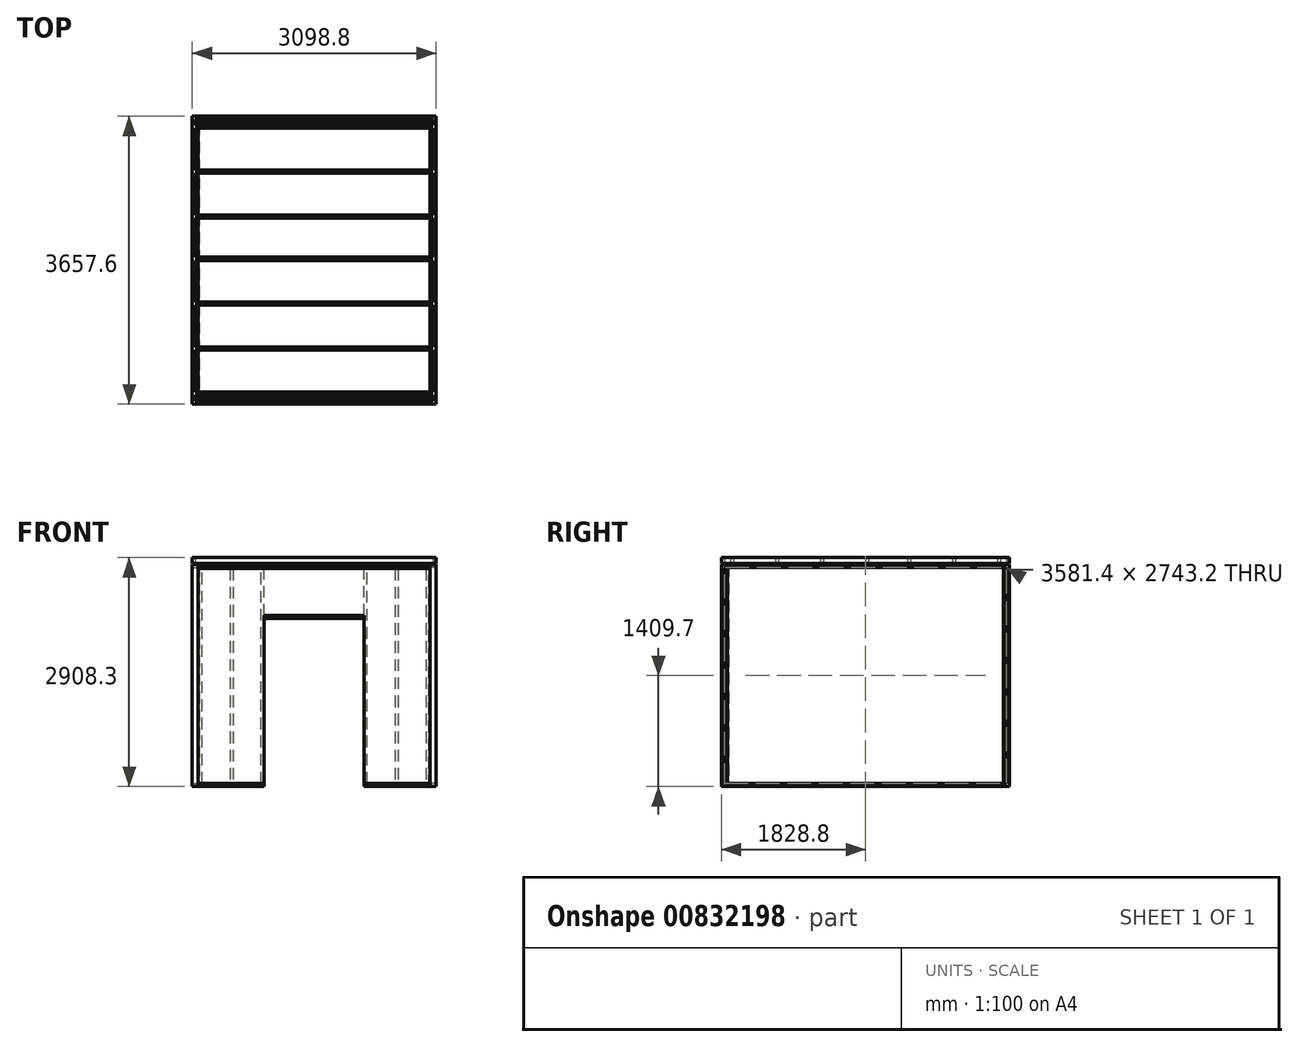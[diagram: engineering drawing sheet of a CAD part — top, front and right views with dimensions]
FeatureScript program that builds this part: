
annotation { "Feature Type Name" : "Feature", "Feature Type Description" : "" }
export const myFeature = defineFeature(function(context is Context, id is Id, definition is map)
    precondition{}
    {
        {
            var Q0;
            Q0=qCreatedBy(makeId("Top.planeOp"),FACE);
            var sketch = newSketch(context, id + "F0", { "sketchPlane" : qUnion([Q0])});
            skLineSegment(sketch, "E0.bottom", {"start": v(-980.79, 2857.66) * mm, "end": v(155.93, 2857.66) * mm});
            skLineSegment(sketch, "E0.top", {"start": v(-980.79, -622.14) * mm, "end": v(1105.1, -622.14) * mm});
            skLineSegment(sketch, "E0.left", {"start": v(-980.79, 2857.66) * mm, "end": v(-980.79, -622.14) * mm});
            skLineSegment(sketch, "E0.right", {"start": v(1940.21, 2857.66) * mm, "end": v(1940.21, -622.14) * mm});
            skLineSegment(sketch, "E1.bottom", {"start": v(-993.49, 2870.36) * mm, "end": v(155.93, 2870.36) * mm});
            skLineSegment(sketch, "E1.top", {"start": v(-993.49, -634.84) * mm, "end": v(913.5, -634.84) * mm});
            skLineSegment(sketch, "E1.left", {"start": v(-993.49, 2870.36) * mm, "end": v(-993.49, -634.84) * mm});
            skLineSegment(sketch, "E1.right", {"start": v(1952.91, 2870.36) * mm, "end": v(1952.91, -634.84) * mm});
            skLineSegment(sketch, "E2.trimOffspring", {"start": v(153.53, 2870.36) * mm, "end": v(1952.91, 2870.36) * mm});
            skLineSegment(sketch, "E3.trimOffspring", {"start": v(149.76, 2857.66) * mm, "end": v(1940.21, 2857.66) * mm});
            skLineSegment(sketch, "E4.trimOffspring", {"start": v(1102.01, -622.14) * mm, "end": v(1940.21, -622.14) * mm});
            skLineSegment(sketch, "E5.trimOffspring", {"start": v(882.21, -634.84) * mm, "end": v(1952.91, -634.84) * mm});
            skSolve(sketch);
        }
        {
            var Q0;
            Q0=makeQuery(id+"F0.imprint","IMPRINT",FACE,{"disambiguationData":[TD([[makeQuery(id+"F0.imprint","IMPRINT",EDGE,{"derivedFrom":sQuery(id+"F0.wireOp",EDGE,"E0.bottom")}),1.0]])]});
            var Q1;
            Q1=makeQuery(id+"F0.imprint","IMPRINT",FACE,{"disambiguationData":[TD([[makeQuery(id+"F0.imprint","IMPRINT",EDGE,{"derivedFrom":sQuery(id+"F0.wireOp",EDGE,"E0.right")}),1.0]])]});
            extrude(context, id + "F1", {"entities" : qUnion([Q0, Q1]), "depth" : 2133.6 * mm + 685.8 * mm, "offsetDistance" : 25.4 * mm});
        }
        {
            var Q0;
            Q0=makeQuery(id+"F1.opExtrude","CAP_FACE",FACE,{"disambiguationData":[OSD([sQuery(id+"F0.wireOp",EDGE,"E0.bottom"),sQuery(id+"F0.wireOp",EDGE,"E0.top"),sQuery(id+"F0.wireOp",EDGE,"E0.left"),sQuery(id+"F0.wireOp",EDGE,"E1.bottom"),sQuery(id+"F0.wireOp",EDGE,"E1.top"),sQuery(id+"F0.wireOp",EDGE,"E1.left"),sQuery(id+"F0.wireOp",EDGE,"ajJvUeQd-ddKz-yDWU-SHTq-AfXzZqwUQA1N.left"),sQuery(id+"F0.wireOp",EDGE,"rDKjrFLu-EuC5-olRp-ZrVZ-GupeaafQM4Xr")])],"isStart":false});
            var sketch = newSketch(context, id + "F2", { "sketchPlane" : qUnion([Q0])});
            skPoint(sketch, "E6.0", {"position": v(1952.91, 2870.36) * mm});
            skPoint(sketch, "E7.0", {"position": v(-993.49, 2870.36) * mm});
            skPoint(sketch, "E8.0", {"position": v(-993.49, -634.84) * mm});
            skLineSegment(sketch, "E9.bottom", {"start": v(-993.49, -634.84) * mm, "end": v(1952.91, -634.84) * mm});
            skLineSegment(sketch, "E9.top", {"start": v(-993.49, 2870.36) * mm, "end": v(1952.91, 2870.36) * mm});
            skLineSegment(sketch, "E9.left", {"start": v(-993.49, -634.84) * mm, "end": v(-993.49, 2870.36) * mm});
            skLineSegment(sketch, "E9.right", {"start": v(1952.91, -634.84) * mm, "end": v(1952.91, 2870.36) * mm});
            skSolve(sketch);
        }
        {
            var Q0;
            Q0=qSketchRegion(id+"F2",true);
            extrude(context, id + "F3", {"entities" : qUnion([Q0]), "depth" : 12.7 * mm, "offsetDistance" : 25.4 * mm});
        }
        {
            var Q0;
            Q0=makeQuery(id+"F1.opExtrude","SWEPT_FACE",FACE,{"disambiguationData":[OSD([sQuery(id+"F0.wireOp",EDGE,"E1.top"),sQuery(id+"F0.wireOp",EDGE,"E5.trimOffspring")])]});
            var sketch = newSketch(context, id + "F4", { "sketchPlane" : qUnion([Q0])});
            skLineSegment(sketch, "E10.bottom", {"start": v(-155.29, 0) * mm, "end": v(1114.71, 0) * mm});
            skLineSegment(sketch, "E10.top", {"start": v(-155.29, 2133.6) * mm, "end": v(1114.71, 2133.6) * mm});
            skLineSegment(sketch, "E10.left", {"start": v(-155.29, 0) * mm, "end": v(-155.29, 2133.6) * mm});
            skLineSegment(sketch, "E10.right", {"start": v(1114.71, 0) * mm, "end": v(1114.71, 2133.6) * mm});
            skSolve(sketch);
        }
        {
            var Q0;
            Q0=makeQuery(id+"F4.imprint","IMPRINT",FACE,{"disambiguationData":[TD([[makeQuery(id+"F4.imprint","IMPRINT",EDGE,{"derivedFrom":sQuery(id+"F4.wireOp",EDGE,"E10.bottom")}),1.0]])]});
            extrude(context, id + "F5", {"entities" : qUnion([Q0]), "operationType" : NewBodyOperationType.REMOVE, "endBound" : BoundingType.THROUGH_ALL, "oppositeDirection" : true, "depth" : 25.4 * mm, "offsetDistance" : 25.4 * mm});
        }
        {
            var Q0;
            Q0=makeQuery(id+"F1.opExtrude","SWEPT_FACE",FACE,{"disambiguationData":[OSD([sQuery(id+"F0.wireOp",EDGE,"E1.top"),sQuery(id+"F0.wireOp",EDGE,"E5.trimOffspring")])]});
            var sketch = newSketch(context, id + "F6", { "sketchPlane" : qUnion([Q0])});
            skLineSegment(sketch, "E11.bottom", {"start": v(-980.79, 0) * mm, "end": v(-155.29, 0) * mm});
            skLineSegment(sketch, "E11.top", {"start": v(-980.79, 38.1) * mm, "end": v(-155.29, 38.1) * mm});
            skLineSegment(sketch, "E11.right", {"start": v(-155.29, 0) * mm, "end": v(-155.29, 38.1) * mm});
            skLineSegment(sketch, "E12.bottom", {"start": v(-980.79, 38.1) * mm, "end": v(-942.69, 38.1) * mm});
            skLineSegment(sketch, "E12.top", {"start": v(-980.79, 2768.6) * mm, "end": v(-942.69, 2768.6) * mm});
            skLineSegment(sketch, "E12.left", {"start": v(-980.79, 38.1) * mm, "end": v(-980.79, 2768.6) * mm});
            skLineSegment(sketch, "E12.right", {"start": v(-942.69, 38.1) * mm, "end": v(-942.69, 2768.6) * mm});
            skLineSegment(sketch, "E13.bottom", {"start": v(-980.79, 2768.6) * mm, "end": v(1940.21, 2768.6) * mm});
            skLineSegment(sketch, "E13.top", {"start": v(-980.79, 2806.7) * mm, "end": v(1940.21, 2806.7) * mm});
            skLineSegment(sketch, "E13.left", {"start": v(-980.79, 2768.6) * mm, "end": v(-980.79, 2806.7) * mm});
            skLineSegment(sketch, "E13.right", {"start": v(1940.21, 2768.6) * mm, "end": v(1940.21, 2806.7) * mm});
            skLineSegment(sketch, "E14.bottom", {"start": v(1940.21, 2768.6) * mm, "end": v(1902.11, 2768.6) * mm});
            skLineSegment(sketch, "E14.top", {"start": v(1940.21, 38.1) * mm, "end": v(1902.11, 38.1) * mm});
            skLineSegment(sketch, "E14.left", {"start": v(1940.21, 2768.6) * mm, "end": v(1940.21, 38.1) * mm});
            skLineSegment(sketch, "E14.right", {"start": v(1902.11, 2768.6) * mm, "end": v(1902.11, 38.1) * mm});
            skLineSegment(sketch, "E15.bottom", {"start": v(1940.21, 38.1) * mm, "end": v(1114.71, 38.1) * mm});
            skLineSegment(sketch, "E15.top", {"start": v(1940.21, 0) * mm, "end": v(1114.71, 0) * mm});
            skLineSegment(sketch, "E15.left", {"start": v(1940.21, 38.1) * mm, "end": v(1940.21, 0) * mm});
            skLineSegment(sketch, "E15.right", {"start": v(1114.71, 38.1) * mm, "end": v(1114.71, 0) * mm});
            skLineSegment(sketch, "E16.bottom", {"start": v(1114.71, 38.1) * mm, "end": v(1152.81, 38.1) * mm});
            skLineSegment(sketch, "E16.top", {"start": v(1114.71, 2768.6) * mm, "end": v(1152.81, 2768.6) * mm});
            skLineSegment(sketch, "E16.left", {"start": v(1114.71, 38.1) * mm, "end": v(1114.71, 2768.6) * mm});
            skLineSegment(sketch, "E16.right", {"start": v(1152.81, 38.1) * mm, "end": v(1152.81, 2768.6) * mm});
            skLineSegment(sketch, "E17.bottom", {"start": v(1114.71, 2133.6) * mm, "end": v(-155.29, 2133.6) * mm});
            skLineSegment(sketch, "E17.top", {"start": v(1114.71, 2171.7) * mm, "end": v(-155.29, 2171.7) * mm});
            skLineSegment(sketch, "E17.left", {"start": v(1114.71, 2133.6) * mm, "end": v(1114.71, 2171.7) * mm});
            skLineSegment(sketch, "E17.right", {"start": v(-155.29, 2133.6) * mm, "end": v(-155.29, 2171.7) * mm});
            skLineSegment(sketch, "E18.bottom", {"start": v(-155.29, 38.1) * mm, "end": v(-193.39, 38.1) * mm});
            skLineSegment(sketch, "E18.top", {"start": v(-155.29, 2768.6) * mm, "end": v(-193.39, 2768.6) * mm});
            skLineSegment(sketch, "E18.left", {"start": v(-155.29, 38.1) * mm, "end": v(-155.29, 2768.6) * mm});
            skLineSegment(sketch, "E18.right", {"start": v(-193.39, 38.1) * mm, "end": v(-193.39, 2768.6) * mm});
            skLineSegment(sketch, "E19.bottom", {"start": v(-587.09, 2768.6) * mm, "end": v(-548.99, 2768.6) * mm});
            skLineSegment(sketch, "E19.top", {"start": v(-587.09, 38.1) * mm, "end": v(-548.99, 38.1) * mm});
            skLineSegment(sketch, "E19.left", {"start": v(-587.09, 2768.6) * mm, "end": v(-587.09, 38.1) * mm});
            skLineSegment(sketch, "E19.right", {"start": v(-548.99, 2768.6) * mm, "end": v(-548.99, 38.1) * mm});
            skLineSegment(sketch, "E20.bottom", {"start": v(1508.41, 2768.6) * mm, "end": v(1546.51, 2768.6) * mm});
            skLineSegment(sketch, "E20.top", {"start": v(1508.41, 38.1) * mm, "end": v(1546.51, 38.1) * mm});
            skLineSegment(sketch, "E20.left", {"start": v(1508.41, 2768.6) * mm, "end": v(1508.41, 38.1) * mm});
            skLineSegment(sketch, "E20.right", {"start": v(1546.51, 2768.6) * mm, "end": v(1546.51, 38.1) * mm});
            skLineSegment(sketch, "E21", {"start": v(-980.79, 38.1) * mm, "end": v(-980.79, 0) * mm});
            skSolve(sketch);
        }
        {
            var Q0;
            Q0=makeQuery(id+"F6.imprint","IMPRINT",FACE,{"disambiguationData":[TD([[makeQuery(id+"F6.imprint","IMPRINT",EDGE,{"derivedFrom":sQuery(id+"F6.wireOp",EDGE,"E13.top")}),-1.0]])]});
            var Q1;
            Q1=makeQuery(id+"F6.imprint","IMPRINT",FACE,{"disambiguationData":[TD([[makeQuery(id+"F6.imprint","IMPRINT",EDGE,{"derivedFrom":sQuery(id+"F6.wireOp",EDGE,"E12.bottom")}),1.0]])]});
            var Q2;
            Q2=makeQuery(id+"F6.imprint","IMPRINT",FACE,{"disambiguationData":[TD([[makeQuery(id+"F6.imprint","IMPRINT",EDGE,{"derivedFrom":sQuery(id+"F6.wireOp",EDGE,"E19.bottom")}),-1.0]])]});
            var Q3;
            {var subQ3=sQuery(id+"F6.wireOp",EDGE,"E18.bottom");Q3=makeQuery(id+"F6.imprint","IMPRINT",FACE,{"disambiguationData":[TD([[makeQuery(id+"F6.imprint","IMPRINT",EDGE,{"derivedFrom":subQ3}),-1.0]])]});}
            var Q4;
            {var subQ0=sQuery(id+"F6.wireOp",EDGE,"E17.bottom");Q4=makeQuery(id+"F6.imprint","IMPRINT",FACE,{"disambiguationData":[TD([[makeQuery(id+"F6.imprint","IMPRINT",EDGE,{"derivedFrom":subQ0}),1.0]])]});}
            var Q5;
            {var subQ3=sQuery(id+"F6.wireOp",EDGE,"E16.bottom");Q5=makeQuery(id+"F6.imprint","IMPRINT",FACE,{"disambiguationData":[TD([[makeQuery(id+"F6.imprint","IMPRINT",EDGE,{"derivedFrom":subQ3}),1.0]])]});}
            var Q6;
            Q6=makeQuery(id+"F6.imprint","IMPRINT",FACE,{"disambiguationData":[TD([[makeQuery(id+"F6.imprint","IMPRINT",EDGE,{"derivedFrom":sQuery(id+"F6.wireOp",EDGE,"E20.bottom")}),-1.0]])]});
            var Q7;
            Q7=makeQuery(id+"F6.imprint","IMPRINT",FACE,{"disambiguationData":[TD([[makeQuery(id+"F6.imprint","IMPRINT",EDGE,{"derivedFrom":sQuery(id+"F6.wireOp",EDGE,"E14.bottom")}),1.0]])]});
            var Q8;
            Q8=makeQuery(id+"F6.imprint","IMPRINT",FACE,{"disambiguationData":[TD([[makeQuery(id+"F6.imprint","IMPRINT",EDGE,{"derivedFrom":sQuery(id+"F6.wireOp",EDGE,"E15.top")}),1.0]])]});
            var Q9;
            Q9=makeQuery(id+"F6.imprint","IMPRINT",FACE,{"disambiguationData":[TD([[makeQuery(id+"F6.imprint","IMPRINT",EDGE,{"derivedFrom":sQuery(id+"F6.wireOp",EDGE,"E11.bottom")}),1.0]])]});
            extrude(context, id + "F7", {"entities" : qUnion([Q0, Q1, Q2, Q3, Q4, Q5, Q6, Q7, Q8, Q9]), "operationType" : NewBodyOperationType.ADD, "depth" : 76.2 * mm, "offsetDistance" : 25.4 * mm});
        }
        {
            var Q0;
            Q0=makeQuery(id+"F1.opExtrude","SWEPT_FACE",FACE,{"disambiguationData":[OSD([sQuery(id+"F0.wireOp",EDGE,"E1.bottom"),sQuery(id+"F0.wireOp",EDGE,"E2.trimOffspring")])]});
            var sketch = newSketch(context, id + "F8", { "sketchPlane" : qUnion([Q0])});
            skLineSegment(sketch, "E22.0", {"start": v(587.09, 2768.6) * mm, "end": v(587.09, 38.1) * mm});
            skLineSegment(sketch, "E22.1", {"start": v(-1114.71, 0) * mm, "end": v(-1114.71, 2133.6) * mm});
            skLineSegment(sketch, "E22.2", {"start": v(548.99, 2768.6) * mm, "end": v(548.99, 38.1) * mm});
            skLineSegment(sketch, "E22.3", {"start": v(-1508.41, 2768.6) * mm, "end": v(-1508.41, 38.1) * mm});
            skLineSegment(sketch, "E22.4", {"start": v(155.29, 0) * mm, "end": v(155.29, 2133.6) * mm});
            skLineSegment(sketch, "E22.5", {"start": v(980.79, 2806.7) * mm, "end": v(-1940.21, 2806.7) * mm});
            skLineSegment(sketch, "E22.6", {"start": v(-1152.81, 38.1) * mm, "end": v(-1152.81, 2768.6) * mm});
            skLineSegment(sketch, "E22.7", {"start": v(-1546.51, 2768.6) * mm, "end": v(-1546.51, 38.1) * mm});
            skLineSegment(sketch, "E22.8", {"start": v(980.79, 0) * mm, "end": v(980.79, 2806.7) * mm});
            skLineSegment(sketch, "E22.9", {"start": v(-1940.21, 0) * mm, "end": v(-1940.21, 2806.7) * mm});
            skLineSegment(sketch, "E22.10", {"start": v(155.29, 2133.6) * mm, "end": v(-1114.71, 2133.6) * mm});
            skLineSegment(sketch, "E22.11", {"start": v(942.69, 38.1) * mm, "end": v(942.69, 2768.6) * mm});
            skLineSegment(sketch, "E22.12", {"start": v(-1902.11, 2768.6) * mm, "end": v(-1902.11, 38.1) * mm});
            skLineSegment(sketch, "E23.0", {"start": v(942.69, 2768.6) * mm, "end": v(587.09, 2768.6) * mm});
            skLineSegment(sketch, "E24.0", {"start": v(548.99, 2768.6) * mm, "end": v(193.39, 2768.6) * mm});
            skLineSegment(sketch, "E25.0", {"start": v(155.29, 2768.6) * mm, "end": v(-1114.71, 2768.6) * mm});
            skLineSegment(sketch, "E26.0.0", {"start": v(155.29, 2171.7) * mm, "end": v(155.29, 2768.6) * mm});
            skLineSegment(sketch, "E26.0.2", {"start": v(155.29, 2768.6) * mm, "end": v(155.29, 2171.7) * mm});
            skLineSegment(sketch, "E27.0.0", {"start": v(-1114.71, 0) * mm, "end": v(-1940.21, 0) * mm});
            skLineSegment(sketch, "E27.0.2", {"start": v(-1940.21, 2806.7) * mm, "end": v(980.79, 2806.7) * mm});
            skLineSegment(sketch, "E27.0.3", {"start": v(980.79, 2806.7) * mm, "end": v(980.79, 0) * mm});
            skLineSegment(sketch, "E27.0.4", {"start": v(980.79, 0) * mm, "end": v(155.29, 0) * mm});
            skLineSegment(sketch, "E27.0.7", {"start": v(-1114.71, 2133.6) * mm, "end": v(-1114.71, 0) * mm});
            skLineSegment(sketch, "E28.0", {"start": v(-1114.71, 2171.7) * mm, "end": v(-1114.71, 2768.6) * mm});
            skLineSegment(sketch, "E29.0", {"start": v(-1114.71, 2171.7) * mm, "end": v(155.29, 2171.7) * mm});
            skLineSegment(sketch, "E30.0.0", {"start": v(193.39, 2768.6) * mm, "end": v(548.99, 2768.6) * mm});
            skLineSegment(sketch, "E30.0.2", {"start": v(548.99, 38.1) * mm, "end": v(193.39, 38.1) * mm});
            skLineSegment(sketch, "E30.0.3", {"start": v(193.39, 38.1) * mm, "end": v(193.39, 2768.6) * mm});
            skLineSegment(sketch, "E31.0", {"start": v(-1152.81, 2768.6) * mm, "end": v(-1508.41, 2768.6) * mm});
            skLineSegment(sketch, "E32.0", {"start": v(-1546.51, 2768.6) * mm, "end": v(-1902.11, 2768.6) * mm});
            skLineSegment(sketch, "E33.0", {"start": v(-1902.11, 38.1) * mm, "end": v(-1546.51, 38.1) * mm});
            skLineSegment(sketch, "E34.0", {"start": v(-1508.41, 38.1) * mm, "end": v(-1152.81, 38.1) * mm});
            skLineSegment(sketch, "E35.0", {"start": v(942.69, 38.1) * mm, "end": v(587.09, 38.1) * mm});
            skSolve(sketch);
        }
        {
            var Q0;
            Q0=qSketchRegion(id+"F8",true);
            extrude(context, id + "F9", {"entities" : qUnion([Q0]), "operationType" : NewBodyOperationType.ADD, "depth" : 76.2 * mm, "offsetDistance" : 25.4 * mm});
        }
        {
            var Q0;
            Q0=makeQuery(id+"F1.opExtrude","SWEPT_FACE",FACE,{"disambiguationData":[OSD([sQuery(id+"F0.wireOp",EDGE,"E1.right")])]});
            var sketch = newSketch(context, id + "F10", { "sketchPlane" : qUnion([Q0])});
            skLineSegment(sketch, "E36.bottom", {"start": v(-711.04, 2819.4) * mm, "end": v(2946.56, 2819.4) * mm});
            skLineSegment(sketch, "E36.top", {"start": v(-711.04, 2781.3) * mm, "end": v(2946.56, 2781.3) * mm});
            skLineSegment(sketch, "E36.left", {"start": v(-711.04, 2819.4) * mm, "end": v(-711.04, 2781.3) * mm});
            skLineSegment(sketch, "E36.right", {"start": v(2946.56, 2819.4) * mm, "end": v(2946.56, 2781.3) * mm});
            skPoint(sketch, "E37.0", {"position": v(2946.56, 2806.7) * mm});
            skPoint(sketch, "E38.0", {"position": v(-711.04, 2806.7) * mm});
            skPoint(sketch, "E39.0", {"position": v(-711.04, 0) * mm});
            skPoint(sketch, "E40.0", {"position": v(2946.56, 0) * mm});
            skLineSegment(sketch, "E41.bottom", {"start": v(2946.56, 0) * mm, "end": v(-711.04, 0) * mm});
            skLineSegment(sketch, "E41.top", {"start": v(2946.56, 38.1) * mm, "end": v(-711.04, 38.1) * mm});
            skLineSegment(sketch, "E41.left", {"start": v(2946.56, 0) * mm, "end": v(2946.56, 38.1) * mm});
            skLineSegment(sketch, "E41.right", {"start": v(-711.04, 0) * mm, "end": v(-711.04, 38.1) * mm});
            skLineSegment(sketch, "E42.bottom", {"start": v(2946.56, 2781.3) * mm, "end": v(2908.46, 2781.3) * mm});
            skLineSegment(sketch, "E42.top", {"start": v(2946.56, 38.1) * mm, "end": v(2908.46, 38.1) * mm});
            skLineSegment(sketch, "E42.left", {"start": v(2946.56, 2781.3) * mm, "end": v(2946.56, 38.1) * mm});
            skLineSegment(sketch, "E42.right", {"start": v(2908.46, 2781.3) * mm, "end": v(2908.46, 38.1) * mm});
            skLineSegment(sketch, "E43.bottom", {"start": v(-711.04, 38.1) * mm, "end": v(-672.94, 38.1) * mm});
            skLineSegment(sketch, "E43.top", {"start": v(-711.04, 2781.3) * mm, "end": v(-672.94, 2781.3) * mm});
            skLineSegment(sketch, "E43.left", {"start": v(-711.04, 38.1) * mm, "end": v(-711.04, 2781.3) * mm});
            skLineSegment(sketch, "E43.right", {"start": v(-672.94, 38.1) * mm, "end": v(-672.94, 2781.3) * mm});
            skLineSegment(sketch, "E44.bottom", {"start": v(-596.74, 2781.3) * mm, "end": v(-558.64, 2781.3) * mm});
            skLineSegment(sketch, "E44.top", {"start": v(-596.74, 38.1) * mm, "end": v(-558.64, 38.1) * mm});
            skLineSegment(sketch, "E44.left", {"start": v(-596.74, 2781.3) * mm, "end": v(-596.74, 38.1) * mm});
            skLineSegment(sketch, "E44.right", {"start": v(-558.64, 2781.3) * mm, "end": v(-558.64, 38.1) * mm});
            skLineSegment(sketch, "E45.bottom", {"start": v(2832.26, 2781.3) * mm, "end": v(2794.16, 2781.3) * mm});
            skLineSegment(sketch, "E45.top", {"start": v(2832.26, 38.1) * mm, "end": v(2794.16, 38.1) * mm});
            skLineSegment(sketch, "E45.left", {"start": v(2832.26, 2781.3) * mm, "end": v(2832.26, 38.1) * mm});
            skLineSegment(sketch, "E45.right", {"start": v(2794.16, 2781.3) * mm, "end": v(2794.16, 38.1) * mm});
            skLineSegment(sketch, "E46.bottom", {"start": v(-25.24, 38.1) * mm, "end": v(12.86, 38.1) * mm});
            skLineSegment(sketch, "E46.top", {"start": v(-25.24, 2781.3) * mm, "end": v(12.86, 2781.3) * mm});
            skLineSegment(sketch, "E46.left", {"start": v(-25.24, 38.1) * mm, "end": v(-25.24, 2781.3) * mm});
            skLineSegment(sketch, "E46.right", {"start": v(12.86, 38.1) * mm, "end": v(12.86, 2781.3) * mm});
            skLineSegment(sketch, "E47.bottom", {"start": v(546.26, 2781.3) * mm, "end": v(584.36, 2781.3) * mm});
            skLineSegment(sketch, "E47.top", {"start": v(546.26, 38.1) * mm, "end": v(584.36, 38.1) * mm});
            skLineSegment(sketch, "E47.left", {"start": v(546.26, 2781.3) * mm, "end": v(546.26, 38.1) * mm});
            skLineSegment(sketch, "E47.right", {"start": v(584.36, 2781.3) * mm, "end": v(584.36, 38.1) * mm});
            skLineSegment(sketch, "E48.bottom", {"start": v(1079.66, 2781.3) * mm, "end": v(1117.76, 2781.3) * mm});
            skLineSegment(sketch, "E48.top", {"start": v(1079.66, 38.1) * mm, "end": v(1117.76, 38.1) * mm});
            skLineSegment(sketch, "E48.left", {"start": v(1079.66, 2781.3) * mm, "end": v(1079.66, 38.1) * mm});
            skLineSegment(sketch, "E48.right", {"start": v(1117.76, 2781.3) * mm, "end": v(1117.76, 38.1) * mm});
            skLineSegment(sketch, "E49.bottom", {"start": v(1651.16, 2781.3) * mm, "end": v(1689.26, 2781.3) * mm});
            skLineSegment(sketch, "E49.top", {"start": v(1651.16, 38.1) * mm, "end": v(1689.26, 38.1) * mm});
            skLineSegment(sketch, "E49.left", {"start": v(1651.16, 2781.3) * mm, "end": v(1651.16, 38.1) * mm});
            skLineSegment(sketch, "E49.right", {"start": v(1689.26, 2781.3) * mm, "end": v(1689.26, 38.1) * mm});
            skLineSegment(sketch, "E50.bottom", {"start": v(2222.66, 2781.3) * mm, "end": v(2260.76, 2781.3) * mm});
            skLineSegment(sketch, "E50.top", {"start": v(2222.66, 38.1) * mm, "end": v(2260.76, 38.1) * mm});
            skLineSegment(sketch, "E50.left", {"start": v(2222.66, 2781.3) * mm, "end": v(2222.66, 38.1) * mm});
            skLineSegment(sketch, "E50.right", {"start": v(2260.76, 2781.3) * mm, "end": v(2260.76, 38.1) * mm});
            skSolve(sketch);
        }
        {
            var Q0;
            Q0=qSketchRegion(id+"F10",true);
            var Q1;
            Q1=makeQuery(id+"F10.imprint","IMPRINT",FACE,{"disambiguationData":[TD([[makeQuery(id+"F10.imprint","IMPRINT",EDGE,{"derivedFrom":sQuery(id+"F10.wireOp",EDGE,"E44.bottom")}),-1.0]])]});
            var Q2;
            Q2=makeQuery(id+"F10.imprint","IMPRINT",FACE,{"disambiguationData":[TD([[makeQuery(id+"F10.imprint","IMPRINT",EDGE,{"derivedFrom":sQuery(id+"F10.wireOp",EDGE,"E46.bottom")}),1.0]])]});
            var Q3;
            Q3=makeQuery(id+"F10.imprint","IMPRINT",FACE,{"disambiguationData":[TD([[makeQuery(id+"F10.imprint","IMPRINT",EDGE,{"derivedFrom":sQuery(id+"F10.wireOp",EDGE,"E47.bottom")}),-1.0]])]});
            var Q4;
            Q4=makeQuery(id+"F10.imprint","IMPRINT",FACE,{"disambiguationData":[TD([[makeQuery(id+"F10.imprint","IMPRINT",EDGE,{"derivedFrom":sQuery(id+"F10.wireOp",EDGE,"E48.bottom")}),-1.0]])]});
            var Q5;
            Q5=makeQuery(id+"F10.imprint","IMPRINT",FACE,{"disambiguationData":[TD([[makeQuery(id+"F10.imprint","IMPRINT",EDGE,{"derivedFrom":sQuery(id+"F10.wireOp",EDGE,"E49.bottom")}),-1.0]])]});
            var Q6;
            Q6=makeQuery(id+"F10.imprint","IMPRINT",FACE,{"disambiguationData":[TD([[makeQuery(id+"F10.imprint","IMPRINT",EDGE,{"derivedFrom":sQuery(id+"F10.wireOp",EDGE,"E50.bottom")}),-1.0]])]});
            var Q7;
            Q7=makeQuery(id+"F10.imprint","IMPRINT",FACE,{"disambiguationData":[TD([[makeQuery(id+"F10.imprint","IMPRINT",EDGE,{"derivedFrom":sQuery(id+"F10.wireOp",EDGE,"E45.bottom")}),1.0]])]});
            extrude(context, id + "F11", {"entities" : qUnion([Q0, Q1, Q2, Q3, Q4, Q5, Q6, Q7]), "operationType" : NewBodyOperationType.ADD, "depth" : 76.2 * mm, "offsetDistance" : 25.4 * mm});
        }
        {
            var Q0;
            Q0=makeQuery(id+"F1.opExtrude","SWEPT_FACE",FACE,{"disambiguationData":[OSD([sQuery(id+"F0.wireOp",EDGE,"E1.left")])]});
            var sketch = newSketch(context, id + "F12", { "sketchPlane" : qUnion([Q0])});
            skLineSegment(sketch, "E51.bottom", {"start": v(-2946.56, 2819.4) * mm, "end": v(711.04, 2819.4) * mm});
            skLineSegment(sketch, "E51.top", {"start": v(-2946.56, 2781.3) * mm, "end": v(711.04, 2781.3) * mm});
            skLineSegment(sketch, "E51.left", {"start": v(-2946.56, 2819.4) * mm, "end": v(-2946.56, 2781.3) * mm});
            skLineSegment(sketch, "E51.right", {"start": v(711.04, 2819.4) * mm, "end": v(711.04, 2781.3) * mm});
            skPoint(sketch, "E52.0", {"position": v(711.04, 2806.7) * mm});
            skPoint(sketch, "E53.0", {"position": v(-2946.56, 0) * mm});
            skPoint(sketch, "E54.0", {"position": v(711.04, 0) * mm});
            skLineSegment(sketch, "E55.bottom", {"start": v(711.04, 0) * mm, "end": v(-2946.56, 0) * mm});
            skLineSegment(sketch, "E55.top", {"start": v(711.04, 38.1) * mm, "end": v(-2946.56, 38.1) * mm});
            skLineSegment(sketch, "E55.left", {"start": v(711.04, 0) * mm, "end": v(711.04, 38.1) * mm});
            skLineSegment(sketch, "E55.right", {"start": v(-2946.56, 0) * mm, "end": v(-2946.56, 38.1) * mm});
            skLineSegment(sketch, "E56.bottom", {"start": v(711.04, 2781.3) * mm, "end": v(672.94, 2781.3) * mm});
            skLineSegment(sketch, "E56.top", {"start": v(711.04, 38.1) * mm, "end": v(672.94, 38.1) * mm});
            skLineSegment(sketch, "E56.left", {"start": v(711.04, 2781.3) * mm, "end": v(711.04, 38.1) * mm});
            skLineSegment(sketch, "E56.right", {"start": v(672.94, 2781.3) * mm, "end": v(672.94, 38.1) * mm});
            skLineSegment(sketch, "E57.bottom", {"start": v(-2946.56, 38.1) * mm, "end": v(-2908.46, 38.1) * mm});
            skLineSegment(sketch, "E57.top", {"start": v(-2946.56, 2781.3) * mm, "end": v(-2908.46, 2781.3) * mm});
            skLineSegment(sketch, "E57.left", {"start": v(-2946.56, 38.1) * mm, "end": v(-2946.56, 2781.3) * mm});
            skLineSegment(sketch, "E57.right", {"start": v(-2908.46, 38.1) * mm, "end": v(-2908.46, 2781.3) * mm});
            skLineSegment(sketch, "E58.bottom", {"start": v(-2832.26, 2781.3) * mm, "end": v(-2794.16, 2781.3) * mm});
            skLineSegment(sketch, "E58.top", {"start": v(-2832.26, 38.1) * mm, "end": v(-2794.16, 38.1) * mm});
            skLineSegment(sketch, "E58.left", {"start": v(-2832.26, 2781.3) * mm, "end": v(-2832.26, 38.1) * mm});
            skLineSegment(sketch, "E58.right", {"start": v(-2794.16, 2781.3) * mm, "end": v(-2794.16, 38.1) * mm});
            skLineSegment(sketch, "E59.bottom", {"start": v(596.74, 2781.3) * mm, "end": v(558.64, 2781.3) * mm});
            skLineSegment(sketch, "E59.top", {"start": v(596.74, 38.1) * mm, "end": v(558.64, 38.1) * mm});
            skLineSegment(sketch, "E59.left", {"start": v(596.74, 2781.3) * mm, "end": v(596.74, 38.1) * mm});
            skLineSegment(sketch, "E59.right", {"start": v(558.64, 2781.3) * mm, "end": v(558.64, 38.1) * mm});
            skLineSegment(sketch, "E60.bottom", {"start": v(-2260.76, 38.1) * mm, "end": v(-2222.66, 38.1) * mm});
            skLineSegment(sketch, "E60.top", {"start": v(-2260.76, 2781.3) * mm, "end": v(-2222.66, 2781.3) * mm});
            skLineSegment(sketch, "E60.left", {"start": v(-2260.76, 38.1) * mm, "end": v(-2260.76, 2781.3) * mm});
            skLineSegment(sketch, "E60.right", {"start": v(-2222.66, 38.1) * mm, "end": v(-2222.66, 2781.3) * mm});
            skLineSegment(sketch, "E61.bottom", {"start": v(-1689.26, 2781.3) * mm, "end": v(-1651.16, 2781.3) * mm});
            skLineSegment(sketch, "E61.top", {"start": v(-1689.26, 38.1) * mm, "end": v(-1651.16, 38.1) * mm});
            skLineSegment(sketch, "E61.left", {"start": v(-1689.26, 2781.3) * mm, "end": v(-1689.26, 38.1) * mm});
            skLineSegment(sketch, "E61.right", {"start": v(-1651.16, 2781.3) * mm, "end": v(-1651.16, 38.1) * mm});
            skLineSegment(sketch, "E62.bottom", {"start": v(-1155.86, 2781.3) * mm, "end": v(-1117.76, 2781.3) * mm});
            skLineSegment(sketch, "E62.top", {"start": v(-1155.86, 38.1) * mm, "end": v(-1117.76, 38.1) * mm});
            skLineSegment(sketch, "E62.left", {"start": v(-1155.86, 2781.3) * mm, "end": v(-1155.86, 38.1) * mm});
            skLineSegment(sketch, "E62.right", {"start": v(-1117.76, 2781.3) * mm, "end": v(-1117.76, 38.1) * mm});
            skLineSegment(sketch, "E63.bottom", {"start": v(-584.36, 2781.3) * mm, "end": v(-546.26, 2781.3) * mm});
            skLineSegment(sketch, "E63.top", {"start": v(-584.36, 38.1) * mm, "end": v(-546.26, 38.1) * mm});
            skLineSegment(sketch, "E63.left", {"start": v(-584.36, 2781.3) * mm, "end": v(-584.36, 38.1) * mm});
            skLineSegment(sketch, "E63.right", {"start": v(-546.26, 2781.3) * mm, "end": v(-546.26, 38.1) * mm});
            skLineSegment(sketch, "E64.bottom", {"start": v(-12.86, 2781.3) * mm, "end": v(25.24, 2781.3) * mm});
            skLineSegment(sketch, "E64.top", {"start": v(-12.86, 38.1) * mm, "end": v(25.24, 38.1) * mm});
            skLineSegment(sketch, "E64.left", {"start": v(-12.86, 2781.3) * mm, "end": v(-12.86, 38.1) * mm});
            skLineSegment(sketch, "E64.right", {"start": v(25.24, 2781.3) * mm, "end": v(25.24, 38.1) * mm});
            skPoint(sketch, "E65.0", {"position": v(-2946.56, 2819.4) * mm});
            skSolve(sketch);
        }
        {
            var Q0;
            Q0=qSketchRegion(id+"F12",true);
            var Q1;
            Q1=makeQuery(id+"F12.imprint","IMPRINT",FACE,{"disambiguationData":[TD([[makeQuery(id+"F12.imprint","IMPRINT",EDGE,{"derivedFrom":sQuery(id+"F12.wireOp",EDGE,"E58.bottom")}),-1.0]])]});
            var Q2;
            Q2=makeQuery(id+"F12.imprint","IMPRINT",FACE,{"disambiguationData":[TD([[makeQuery(id+"F12.imprint","IMPRINT",EDGE,{"derivedFrom":sQuery(id+"F12.wireOp",EDGE,"E60.bottom")}),1.0]])]});
            var Q3;
            Q3=makeQuery(id+"F12.imprint","IMPRINT",FACE,{"disambiguationData":[TD([[makeQuery(id+"F12.imprint","IMPRINT",EDGE,{"derivedFrom":sQuery(id+"F12.wireOp",EDGE,"E61.bottom")}),-1.0]])]});
            var Q4;
            Q4=makeQuery(id+"F12.imprint","IMPRINT",FACE,{"disambiguationData":[TD([[makeQuery(id+"F12.imprint","IMPRINT",EDGE,{"derivedFrom":sQuery(id+"F12.wireOp",EDGE,"E62.bottom")}),-1.0]])]});
            var Q5;
            Q5=makeQuery(id+"F12.imprint","IMPRINT",FACE,{"disambiguationData":[TD([[makeQuery(id+"F12.imprint","IMPRINT",EDGE,{"derivedFrom":sQuery(id+"F12.wireOp",EDGE,"E63.bottom")}),-1.0]])]});
            var Q6;
            Q6=makeQuery(id+"F12.imprint","IMPRINT",FACE,{"disambiguationData":[TD([[makeQuery(id+"F12.imprint","IMPRINT",EDGE,{"derivedFrom":sQuery(id+"F12.wireOp",EDGE,"E64.bottom")}),-1.0]])]});
            var Q7;
            Q7=makeQuery(id+"F12.imprint","IMPRINT",FACE,{"disambiguationData":[TD([[makeQuery(id+"F12.imprint","IMPRINT",EDGE,{"derivedFrom":sQuery(id+"F12.wireOp",EDGE,"E59.bottom")}),1.0]])]});
            extrude(context, id + "F13", {"entities" : qUnion([Q0, Q1, Q2, Q3, Q4, Q5, Q6, Q7]), "operationType" : NewBodyOperationType.ADD, "depth" : 76.2 * mm, "offsetDistance" : 25.4 * mm});
        }
        {
            var Q0;
            Q0=makeQuery(id+"F3.opExtrude","CAP_FACE",FACE,{"disambiguationData":[OSD([sQuery(id+"F2.wireOp",EDGE,"E9.bottom"),sQuery(id+"F2.wireOp",EDGE,"E9.top"),sQuery(id+"F2.wireOp",EDGE,"E9.left"),sQuery(id+"F2.wireOp",EDGE,"E9.right")])],"isStart":false});
            var sketch = newSketch(context, id + "F14", { "sketchPlane" : qUnion([Q0])});
            skPoint(sketch, "E66.0", {"position": v(-1069.69, 2946.56) * mm});
            skPoint(sketch, "E67.0", {"position": v(2029.11, -711.04) * mm});
            skLineSegment(sketch, "E68.bottom", {"start": v(2029.11, -711.04) * mm, "end": v(-1069.69, -711.04) * mm});
            skLineSegment(sketch, "E68.top", {"start": v(2029.11, 2946.56) * mm, "end": v(-1069.69, 2946.56) * mm});
            skLineSegment(sketch, "E68.left", {"start": v(2029.11, -711.04) * mm, "end": v(2029.11, 2946.56) * mm});
            skLineSegment(sketch, "E68.right", {"start": v(-1069.69, -711.04) * mm, "end": v(-1069.69, 2946.56) * mm});
            skLineSegment(sketch, "E69.bottom", {"start": v(-1031.59, 2906.43) * mm, "end": v(1991.01, 2906.43) * mm});
            skLineSegment(sketch, "E69.top", {"start": v(-1031.59, -672.94) * mm, "end": v(1991.01, -672.94) * mm});
            skLineSegment(sketch, "E69.left", {"start": v(-1031.59, 2906.43) * mm, "end": v(-1031.59, 2832.26) * mm});
            skLineSegment(sketch, "E69.right", {"start": v(1991.01, 2906.43) * mm, "end": v(1991.01, 2832.26) * mm});
            skPoint(sketch, "E70.0", {"position": v(-1069.69, 2260.76) * mm});
            skPoint(sketch, "E71.0", {"position": v(-1069.69, 1689.26) * mm});
            skPoint(sketch, "E72.0", {"position": v(-1069.69, 1155.86) * mm});
            skPoint(sketch, "E73.0", {"position": v(-1069.69, 584.36) * mm});
            skPoint(sketch, "E74.0", {"position": v(-1069.69, 546.26) * mm});
            skPoint(sketch, "E75.0", {"position": v(-1069.69, 1117.76) * mm});
            skPoint(sketch, "E76.0", {"position": v(-1069.69, 1651.16) * mm});
            skPoint(sketch, "E77.0", {"position": v(-1069.69, 2222.66) * mm});
            skPoint(sketch, "E78.0", {"position": v(-1069.69, 2832.26) * mm});
            skPoint(sketch, "E79.0", {"position": v(-1069.69, 2794.16) * mm});
            skPoint(sketch, "E80.0", {"position": v(-1069.69, 12.86) * mm});
            skPoint(sketch, "E81.0", {"position": v(-1069.69, -25.24) * mm});
            skPoint(sketch, "E82.0", {"position": v(-1069.69, -558.64) * mm});
            skPoint(sketch, "E83.0", {"position": v(-1069.69, -596.74) * mm});
            skLineSegment(sketch, "E84.bottom", {"start": v(-1031.59, 2832.26) * mm, "end": v(1991.01, 2832.26) * mm});
            skLineSegment(sketch, "E84.top", {"start": v(-1031.59, 2794.16) * mm, "end": v(1991.01, 2794.16) * mm});
            skLineSegment(sketch, "E84.left", {"start": v(-1069.69, 2832.26) * mm, "end": v(-1069.69, 2794.16) * mm});
            skLineSegment(sketch, "E84.right", {"start": v(2029.11, 2832.26) * mm, "end": v(2029.11, 2794.16) * mm});
            skLineSegment(sketch, "E85.bottom", {"start": v(-1031.59, 2260.76) * mm, "end": v(1991.01, 2260.76) * mm});
            skLineSegment(sketch, "E85.top", {"start": v(-1031.59, 2222.66) * mm, "end": v(1991.01, 2222.66) * mm});
            skLineSegment(sketch, "E85.left", {"start": v(-1069.69, 2260.76) * mm, "end": v(-1069.69, 2222.66) * mm});
            skLineSegment(sketch, "E85.right", {"start": v(2029.11, 2260.76) * mm, "end": v(2029.11, 2222.66) * mm});
            skLineSegment(sketch, "E86.bottom", {"start": v(-1031.59, 1689.26) * mm, "end": v(1991.01, 1689.26) * mm});
            skLineSegment(sketch, "E86.top", {"start": v(-1031.59, 1651.16) * mm, "end": v(1991.01, 1651.16) * mm});
            skLineSegment(sketch, "E86.left", {"start": v(-1069.69, 1689.26) * mm, "end": v(-1069.69, 1651.16) * mm});
            skLineSegment(sketch, "E86.right", {"start": v(2029.11, 1689.26) * mm, "end": v(2029.11, 1651.16) * mm});
            skPoint(sketch, "E87.oppositeSnap0", {"position": v(1991.01, 1116.74) * mm});
            skLineSegment(sketch, "E87.bottom", {"start": v(-1031.59, 1155.86) * mm, "end": v(1991.01, 1155.86) * mm});
            skLineSegment(sketch, "E87.top", {"start": v(-1031.59, 1116.74) * mm, "end": v(1991.01, 1116.74) * mm});
            skLineSegment(sketch, "E87.left", {"start": v(-1069.69, 1155.86) * mm, "end": v(-1069.69, 1116.74) * mm});
            skLineSegment(sketch, "E87.right", {"start": v(2029.11, 1155.86) * mm, "end": v(2029.11, 1116.74) * mm});
            skLineSegment(sketch, "E88.bottom", {"start": v(-1031.59, -558.64) * mm, "end": v(1991.01, -558.64) * mm});
            skLineSegment(sketch, "E88.top", {"start": v(-1031.59, -596.74) * mm, "end": v(1991.01, -596.74) * mm});
            skLineSegment(sketch, "E88.left", {"start": v(-1069.69, -558.64) * mm, "end": v(-1069.69, -596.74) * mm});
            skLineSegment(sketch, "E88.right", {"start": v(2029.11, -558.64) * mm, "end": v(2029.11, -596.74) * mm});
            skLineSegment(sketch, "E89.bottom", {"start": v(-1031.59, -25.24) * mm, "end": v(1991.01, -25.24) * mm});
            skLineSegment(sketch, "E89.top", {"start": v(-1031.59, 12.86) * mm, "end": v(1991.01, 12.86) * mm});
            skLineSegment(sketch, "E89.left", {"start": v(-1069.69, -25.24) * mm, "end": v(-1069.69, 12.86) * mm});
            skLineSegment(sketch, "E89.right", {"start": v(2029.11, -25.24) * mm, "end": v(2029.11, 12.86) * mm});
            skLineSegment(sketch, "E90.bottom", {"start": v(-1031.59, 546.26) * mm, "end": v(1991.01, 546.26) * mm});
            skLineSegment(sketch, "E90.top", {"start": v(-1031.59, 584.36) * mm, "end": v(1991.01, 584.36) * mm});
            skLineSegment(sketch, "E90.left", {"start": v(-1069.69, 546.26) * mm, "end": v(-1069.69, 584.36) * mm});
            skLineSegment(sketch, "E90.right", {"start": v(2029.11, 546.26) * mm, "end": v(2029.11, 584.36) * mm});
            skLineSegment(sketch, "E91.trimOffspring", {"start": v(-1031.59, -596.74) * mm, "end": v(-1031.59, -672.94) * mm});
            skLineSegment(sketch, "E92.trimOffspring", {"start": v(-1031.59, -25.24) * mm, "end": v(-1031.59, -558.64) * mm});
            skLineSegment(sketch, "E93.trimOffspring", {"start": v(-1031.59, 546.26) * mm, "end": v(-1031.59, 12.86) * mm});
            skLineSegment(sketch, "E94.trimOffspring", {"start": v(-1031.59, 1116.74) * mm, "end": v(-1031.59, 584.36) * mm});
            skLineSegment(sketch, "E95.trimOffspring", {"start": v(-1031.59, 1651.16) * mm, "end": v(-1031.59, 1155.86) * mm});
            skLineSegment(sketch, "E96.trimOffspring", {"start": v(-1031.59, 2222.66) * mm, "end": v(-1031.59, 1689.26) * mm});
            skLineSegment(sketch, "E97.trimOffspring", {"start": v(-1031.59, 2794.16) * mm, "end": v(-1031.59, 2260.76) * mm});
            skLineSegment(sketch, "E98.trimOffspring", {"start": v(1991.01, 2794.16) * mm, "end": v(1991.01, 2260.76) * mm});
            skLineSegment(sketch, "E99.trimOffspring", {"start": v(1991.01, 2222.66) * mm, "end": v(1991.01, 1689.26) * mm});
            skLineSegment(sketch, "E100.trimOffspring", {"start": v(1991.01, 1651.16) * mm, "end": v(1991.01, 1155.86) * mm});
            skLineSegment(sketch, "E101.trimOffspring", {"start": v(1991.01, 1116.74) * mm, "end": v(1991.01, 584.36) * mm});
            skLineSegment(sketch, "E102.trimOffspring", {"start": v(1991.01, 546.26) * mm, "end": v(1991.01, 12.86) * mm});
            skLineSegment(sketch, "E103.trimOffspring", {"start": v(1991.01, -25.24) * mm, "end": v(1991.01, -558.64) * mm});
            skLineSegment(sketch, "E104.trimOffspring", {"start": v(1991.01, -596.74) * mm, "end": v(1991.01, -672.94) * mm});
            skSolve(sketch);
        }
        {
            var Q0;
            Q0=qSketchRegion(id+"F14",true);
            extrude(context, id + "F15", {"entities" : qUnion([Q0]), "operationType" : NewBodyOperationType.ADD, "depth" : 76.2 * mm, "offsetDistance" : 25.4 * mm});
        }
    });
